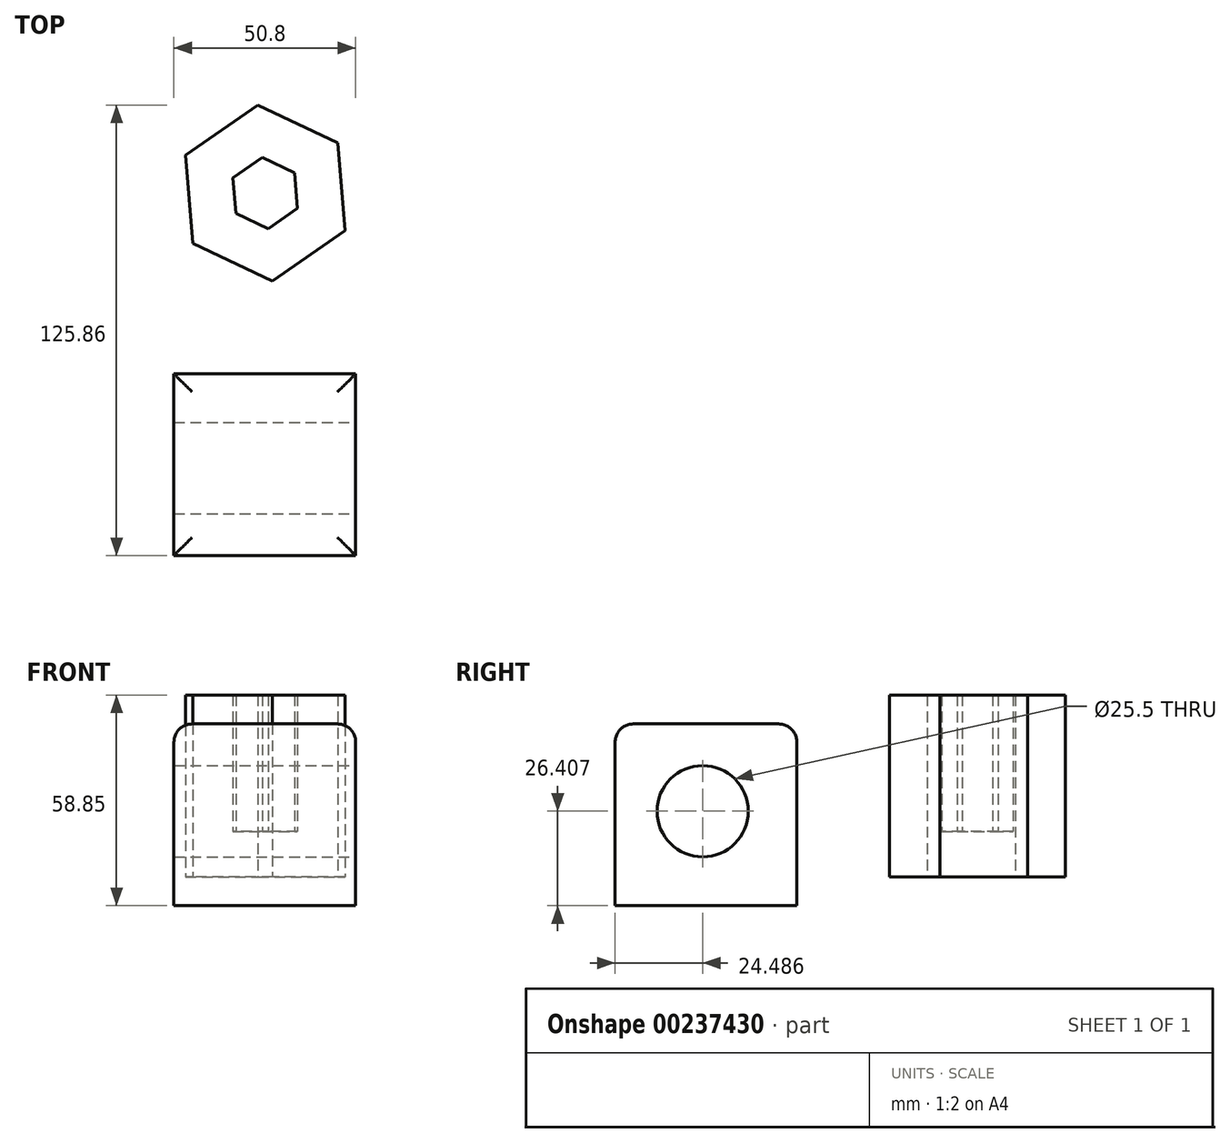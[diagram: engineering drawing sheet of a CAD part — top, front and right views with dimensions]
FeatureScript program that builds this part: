
annotation { "Feature Type Name" : "Feature", "Feature Type Description" : "" }
export const myFeature = defineFeature(function(context is Context, id is Id, definition is map)
    precondition{}
    {
        {
            var Q0;
            Q0=qCreatedBy(makeId("Front.planeOp"),FACE);
            var sketch = newSketch(context, id + "F0", { "sketchPlane" : qUnion([Q0])});
            skLineSegment(sketch, "E0.bottom", {"start": v(-50.8, 42.75) * mm, "end": v(0, 42.75) * mm});
            skLineSegment(sketch, "E0.top", {"start": v(-50.8, -8.05) * mm, "end": v(0, -8.05) * mm});
            skLineSegment(sketch, "E0.left", {"start": v(-50.8, 42.75) * mm, "end": v(-50.8, -8.05) * mm});
            skLineSegment(sketch, "E0.right", {"start": v(0, 42.75) * mm, "end": v(0, -8.05) * mm});
            skSolve(sketch);
        }
        {
            var Q0;
            Q0=makeQuery(id+"F0.imprint","IMPRINT",FACE,{"disambiguationData":[TD([[makeQuery(id+"F0.imprint","IMPRINT",EDGE,{"derivedFrom":sQuery(id+"F0.wireOp",EDGE,"E0.bottom")}),-1.0]])]});
            extrude(context, id + "F1", {"entities" : qUnion([Q0]), "depth" : 50.8 * mm});
        }
        {
            var Q0;
            Q0=makeQuery(id+"F1.opExtrude","SWEPT_EDGE",EDGE,{"disambiguationData":[OSD([sQuery(id+"F0.wireOp",EDGE,"E0.bottom"),sQuery(id+"F0.wireOp",EDGE,"E0.right")])]});
            var Q1;
            Q1=makeQuery(id+"F1.opExtrude","CAP_EDGE",EDGE,{"disambiguationData":[OSD([sQuery(id+"F0.wireOp",EDGE,"E0.bottom")])],"isStart":false});
            var Q2;
            Q2=makeQuery(id+"F1.opExtrude","SWEPT_EDGE",EDGE,{"disambiguationData":[OSD([sQuery(id+"F0.wireOp",EDGE,"E0.bottom"),sQuery(id+"F0.wireOp",EDGE,"E0.left")])]});
            var Q3;
            Q3=makeQuery(id+"F1.opExtrude","CAP_EDGE",EDGE,{"disambiguationData":[OSD([sQuery(id+"F0.wireOp",EDGE,"E0.bottom")])],"isStart":true});
            fillet(context, id + "F2", {"entities" : qUnion([Q0, Q1, Q2, Q3]), "radius" : 5.08 * mm, "tangentPropagation" : true, "allowEdgeOverflow" : false});
        }
        {
            var Q0;
            Q0=makeQuery(id+"F1.opExtrude","SWEPT_FACE",FACE,{"disambiguationData":[OSD([sQuery(id+"F0.wireOp",EDGE,"E0.right")])]});
            var sketch = newSketch(context, id + "F3", { "sketchPlane" : qUnion([Q0])});
            skCircle(sketch, "E1", {"center": v(-26.31, 18.36) * mm, "radius": 12.75 * mm});
            skSolve(sketch);
        }
        {
            var Q0;
            Q0=makeQuery(id+"F3.imprint","IMPRINT",FACE,{"disambiguationData":[TD([[makeQuery(id+"F3.imprint","IMPRINT",EDGE,{"derivedFrom":sQuery(id+"F3.wireOp",EDGE,"E1")}),1.0]])]});
            extrude(context, id + "F4", {"entities" : qUnion([Q0]), "operationType" : NewBodyOperationType.REMOVE, "endBound" : BoundingType.THROUGH_ALL, "oppositeDirection" : true, "depth" : 25.4 * mm});
        }
        {
            var Q0;
            Q0=qCreatedBy(makeId("Top.planeOp"),FACE);
            var sketch = newSketch(context, id + "F5", { "sketchPlane" : qUnion([Q0])});
            skCircle(sketch, "E2.cCircle", {"center": v(-25.3, 50.5) * mm, "radius": 24.64 * mm, "construction": true});
            skLineSegment(sketch, "E2.0", {"start": v(-23.28, 25.94) * mm, "end": v(-45.56, 36.47) * mm});
            skLineSegment(sketch, "E2.1", {"start": v(-45.56, 36.47) * mm, "end": v(-47.57, 61.03) * mm});
            skLineSegment(sketch, "E2.2", {"start": v(-47.57, 61.03) * mm, "end": v(-27.31, 75.06) * mm});
            skLineSegment(sketch, "E2.3", {"start": v(-27.31, 75.06) * mm, "end": v(-5.03, 64.53) * mm});
            skLineSegment(sketch, "E2.4", {"start": v(-5.03, 64.53) * mm, "end": v(-3.02, 39.96) * mm});
            skLineSegment(sketch, "E2.5", {"start": v(-3.02, 39.96) * mm, "end": v(-23.28, 25.94) * mm});
            skSolve(sketch);
        }
        {
            var Q0;
            Q0 = qSketchRegion(id + "F5", true);
            extrude(context, id + "F6", {"entities" : qUnion([Q0]), "depth" : 50.8 * mm});
        }
        {
            var Q0;
            Q0=makeQuery(id+"F6.opExtrude","CAP_FACE",FACE,{"disambiguationData":[OSD([sQuery(id+"F5.wireOp",EDGE,"E2.0"),sQuery(id+"F5.wireOp",EDGE,"E2.1"),sQuery(id+"F5.wireOp",EDGE,"E2.2"),sQuery(id+"F5.wireOp",EDGE,"E2.3"),sQuery(id+"F5.wireOp",EDGE,"E2.4"),sQuery(id+"F5.wireOp",EDGE,"E2.5")])],"isStart":false});
            shell(context, id + "F7", {"entities" : qUnion([Q0]), "thickness" : 12.7 * mm});
        }
    });
